# Revit family: bimlib_narujnyeblokisistemakondicionirovaniya_mrv-iii-s_seriyaav_haier
name_source: partatom
category: Оборудование
units: mm (PartAtom-declared; Revit-internal decimal feet)

## family parameters
Всегда вертикально = Да
На основе рабочей плоскости = Нет
Общий = Нет
При загрузке вырезать с полостями = Нет
Размер круглого соединителя = Использовать диаметр
Тип детали = Нормальный
Точка расчета площади = Нет

## types (3) — shared parameters
ADSK_URL документации изделия = https://haierproff.ru
ADSK_URL страницы изделия = https://haierproff.ru
ADSK_Версия Revit = 2017
ADSK_Группирование = VRF-системы MRV III - S'' серия AV
ADSK_Единица измерения = шт.
ADSK_Завод-изготовитель = Haier Group
ADSK_Классификация нагрузок = ОВК
ADSK_Количество = 1
ADSK_Количество фаз = 3
ADSK_Коэффициент мощности = 1
ADSK_Масса = 168
ADSK_Напряжение = 400 В
ADSK_Обозначение = MRV III - S'' серия AV
ADSK_Размер_Высота = 1636 мм
ADSK_Размер_Глубина = 400 мм
ADSK_Размер_Ширина = 1050 мм
ADSK_Расход воздуха = 10000.0 м³/ч
BL_BIM library = https://bimlib.pro
HG_URL поставщика = www.haierproff.ru
URL = www.haier.com
Диаметр_Газ = 19.05 мм
Заправка хладагента = 6.10 кг
Изготовитель = Haier Group
Производитель компрессора = MITSUBISHI ELECTRIC
Работа на обогрев = Нет
Рабочий диапазон_Обогрев = -20 ~ 27
Рабочий диапазон_Охлаждение = -5 ~ 48
Сбоку = Подключение : Сбоку
Сзади = Подключение : Сзади
Снизу = Подключение : Снизу
Спереди = Подключение : Спереди
Тип компрессора = Роторный
Тип хладагента = R410A
Частота тока = 50 Гц
zero-valued in all types: Отметка по умолчанию

## per-type parameters (varying)
| type | ADSK_Код изделия | ADSK_Наименование | ADSK_Наименование краткое | ADSK_Номинальная мощность | ADSK_Полная мощность | Диаметр_Жидкость | Звуковая мощность | Звуковое давление | Обогрев_Потребляемая мощность | Охлаждение_Потребляемая мощность | Теплопроизводительность | Холодопроизводительность |
| AV08NMSETA_8HP_HAIER | AV08NMSETA | Наружный блок VRF-системы кондиционирования MRV III - S'' серия AV, 8HP | VRF-системы MRV MRV III - S'' серия AV, 8HP | 5790 Вт | 5790 В·А | 9.52 мм | 66 | 55 | 5 кВт | 6 кВт | 25 кВт | 23 кВт |
| AV10NMSETA_10HP_HAIER | AV10NMSETA | Наружный блок VRF-системы кондиционирования MRV III - S'' серия AV, 10HP | VRF-системы MRV MRV III - S'' серия AV, 10HP | 8000 Вт | 8000 В·А | 12.7 мм | 69 | 58 | 8 кВт | 8 кВт | 32 кВт | 28 кВт |
| AV12NMSETA_12HP_HAIER | AV12NMSETA | Наружный блок VRF-системы кондиционирования MRV III - S'' серия AV, 12HP | VRF-системы MRV MRV III - S'' серия AV, 12HP | 9750 Вт | 9750 В·А | 12.7 мм | 71 | 60 | 10 кВт | 10 кВт | 38 кВт | 34 кВт |
